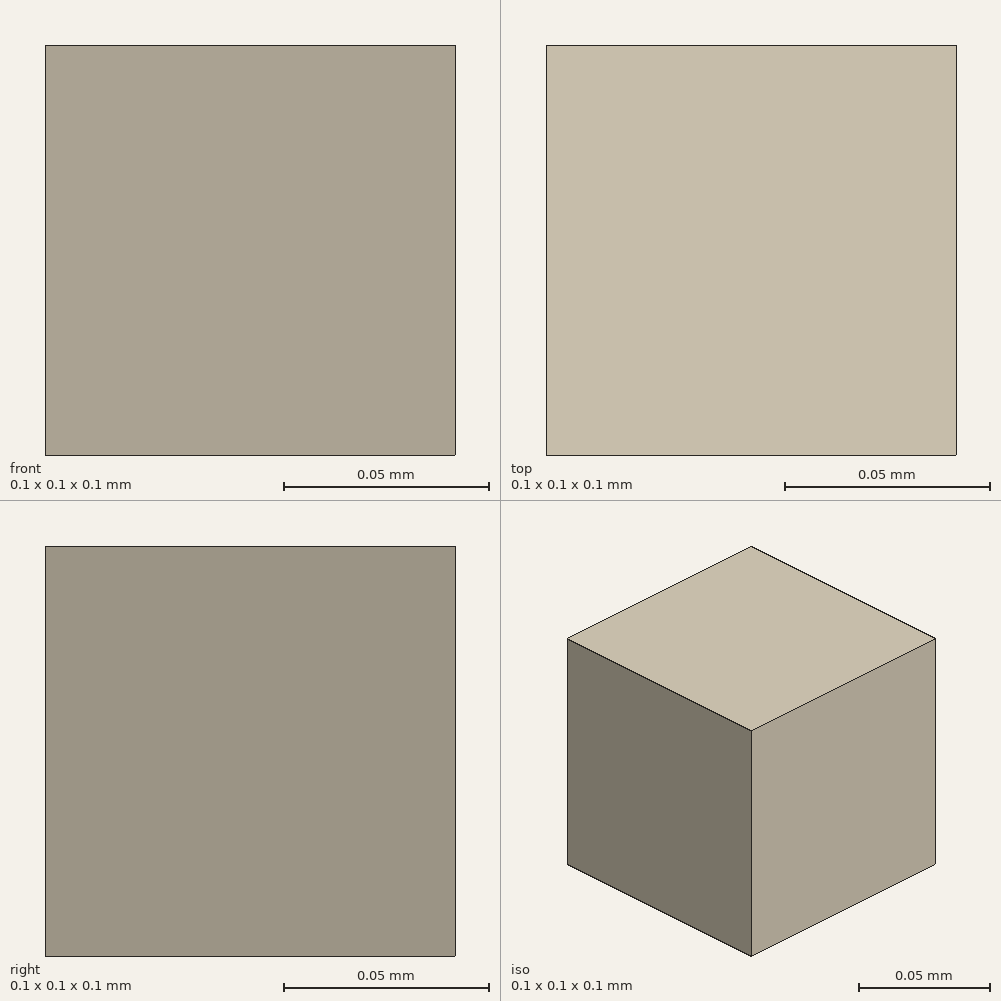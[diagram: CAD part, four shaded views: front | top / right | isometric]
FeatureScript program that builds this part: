
annotation { "Feature Type Name" : "Feature", "Feature Type Description" : "" }
export const myFeature = defineFeature(function(context is Context, id is Id, definition is map)
    precondition{}
    {
        {
            var Q0;
            Q0=qCreatedBy(makeId("Top.planeOp"),FACE);
            var sketch = newSketch(context, id + "F0", { "sketchPlane" : qUnion([Q0])});
            skLineSegment(sketch, "E0.bottom", {"start": v(0, 0) * mm, "end": v(0.1, 0) * mm});
            skLineSegment(sketch, "E0.top", {"start": v(0, -0.1) * mm, "end": v(0.1, -0.1) * mm});
            skLineSegment(sketch, "E0.left", {"start": v(0, 0) * mm, "end": v(0, -0.1) * mm});
            skLineSegment(sketch, "E0.right", {"start": v(0.1, 0) * mm, "end": v(0.1, -0.1) * mm});
            skSolve(sketch);
        }
        {
            var Q0;
            Q0=makeQuery(id+"F0.imprint","IMPRINT",FACE,{"disambiguationData":[TD([[makeQuery(id+"F0.imprint","IMPRINT",EDGE,{"derivedFrom":sQuery(id+"F0.wireOp",EDGE,"E0.bottom")}),-1.0]])]});
            extrude(context, id + "F1", {"entities" : qUnion([Q0]), "depth" : .1 * mm, "offsetDistance" : 25 * mm});
        }
    });
